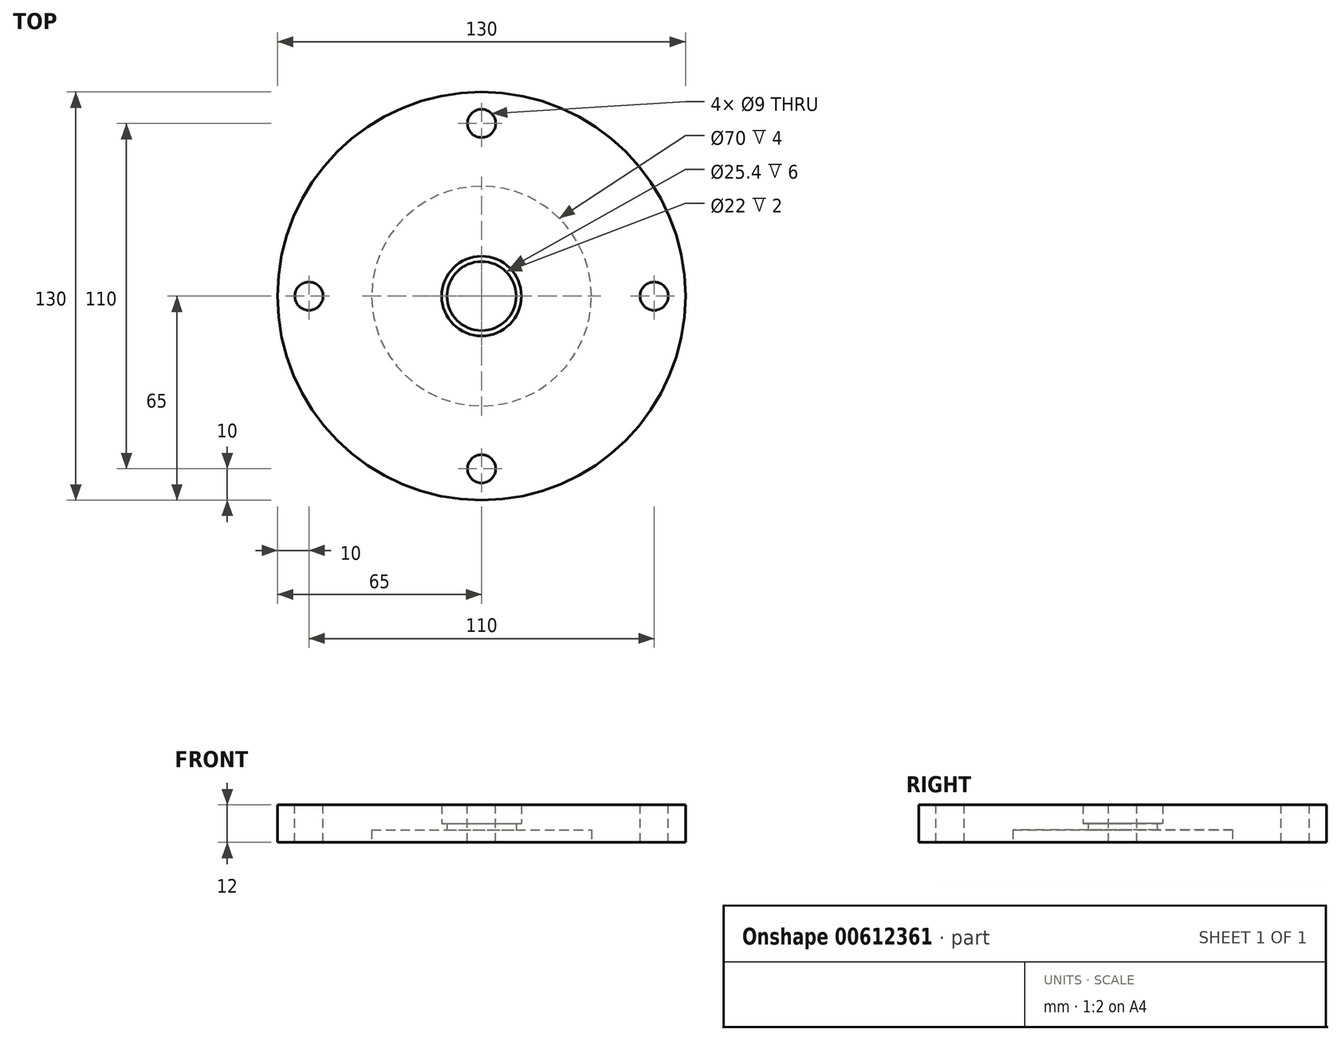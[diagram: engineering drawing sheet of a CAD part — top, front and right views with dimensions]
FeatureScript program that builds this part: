
annotation { "Feature Type Name" : "Feature", "Feature Type Description" : "" }
export const myFeature = defineFeature(function(context is Context, id is Id, definition is map)
    precondition{}
    {
        {
            var Q0;
            Q0=qCreatedBy(makeId("Front.planeOp"),FACE);
            var sketch = newSketch(context, id + "F0", { "sketchPlane" : qUnion([Q0])});
            skLineSegment(sketch, "E0", {"start": v(0, 0) * mm, "end": v(0, 17.2) * mm});
            skLineSegment(sketch, "E1", {"start": v(35, 0) * mm, "end": v(65, 0) * mm});
            skLineSegment(sketch, "E2", {"start": v(65, 0) * mm, "end": v(65, 12) * mm});
            skLineSegment(sketch, "E3", {"start": v(65, 12) * mm, "end": v(12.7, 12) * mm});
            skLineSegment(sketch, "E4", {"start": v(12.7, 12) * mm, "end": v(12.7, 6) * mm});
            skLineSegment(sketch, "E5", {"start": v(11, 6) * mm, "end": v(12.7, 6) * mm});
            skLineSegment(sketch, "E6", {"start": v(11, 6) * mm, "end": v(11, 4) * mm});
            skLineSegment(sketch, "E7", {"start": v(35, 4) * mm, "end": v(11, 4) * mm});
            skLineSegment(sketch, "E8", {"start": v(35, 4) * mm, "end": v(35, 0) * mm});
            skSolve(sketch);
        }
        {
            var Q0;
            Q0=makeQuery(id+"F0.imprint","IMPRINT",FACE,{"disambiguationData":[TD([[makeQuery(id+"F0.imprint","IMPRINT",EDGE,{"derivedFrom":sQuery(id+"F0.wireOp",EDGE,"E1")}),1.0]])]});
            var Q1;
            Q1=sQuery(id+"F0.wireOp",EDGE,"E0");
            revolve(context, id + "F1", {"entities" : qUnion([Q0]), "axis" : qUnion([Q1]), "revolveType" : RevolveType.FULL});
        }
        {
            var Q0;
            Q0=makeQuery(id+"F1.opRevolve","SWEPT_FACE",FACE,{"disambiguationData":[OSD([sQuery(id+"F0.wireOp",EDGE,"E3")])]});
            var sketch = newSketch(context, id + "F2", { "sketchPlane" : qUnion([Q0])});
            skArc(sketch, "E9", {"start": v(54.82, 4.5) * mm, "mid": v(38.9, 38.9) * mm, "end": v(4.5, 54.82) * mm});
            skCircle(sketch, "E10", {"center": v(55, 0) * mm, "radius": 4.5 * mm});
            skCircle(sketch, "E11.1.0", {"center": v(0, 55) * mm, "radius": 4.5 * mm});
            skCircle(sketch, "E11.2.0", {"center": v(-55, 0) * mm, "radius": 4.5 * mm});
            skCircle(sketch, "E11.3.0", {"center": v(0, -55) * mm, "radius": 4.5 * mm});
            skArc(sketch, "E12.trimOffspring", {"start": v(-4.5, 54.82) * mm, "mid": v(-38.9, 38.9) * mm, "end": v(-54.82, 4.5) * mm});
            skArc(sketch, "E13.trimOffspring", {"start": v(-54.82, -4.5) * mm, "mid": v(-38.9, -38.9) * mm, "end": v(-4.5, -54.82) * mm});
            skArc(sketch, "E14.trimOffspring", {"start": v(4.5, -54.82) * mm, "mid": v(38.9, -38.9) * mm, "end": v(54.82, -4.5) * mm});
            skSolve(sketch);
        }
        {
            var Q0;
            {var subQ0=sQuery(id+"F2.wireOp",EDGE,"E11.1.0");var subQ1=makeQuery(id+"F2.imprint","INTERSECT",VERTEX,{"derivedFrom":[sQuery(id+"F2.wireOp",EDGE,"E9"),subQ0]});Q0=makeQuery(id+"F2.imprint","IMPRINT",FACE,{"disambiguationData":[TD([[makeQuery(id+"F2.imprint","IMPRINT",EDGE,{"disambiguationData":[TD([[subQ1,1.0]])],"derivedFrom":subQ0}),1.0]])]});}
            var Q1;
            {var subQ0=sQuery(id+"F2.wireOp",EDGE,"E11.2.0");var subQ1=makeQuery(id+"F2.imprint","INTERSECT",VERTEX,{"derivedFrom":[subQ0,sQuery(id+"F2.wireOp",EDGE,"E12.trimOffspring")]});Q1=makeQuery(id+"F2.imprint","IMPRINT",FACE,{"disambiguationData":[TD([[makeQuery(id+"F2.imprint","IMPRINT",EDGE,{"disambiguationData":[TD([[subQ1,1.0]])],"derivedFrom":subQ0}),1.0]])]});}
            var Q2;
            {var subQ0=sQuery(id+"F2.wireOp",EDGE,"E11.3.0");var subQ1=makeQuery(id+"F2.imprint","INTERSECT",VERTEX,{"derivedFrom":[subQ0,sQuery(id+"F2.wireOp",EDGE,"E13.trimOffspring")]});Q2=makeQuery(id+"F2.imprint","IMPRINT",FACE,{"disambiguationData":[TD([[makeQuery(id+"F2.imprint","IMPRINT",EDGE,{"disambiguationData":[TD([[subQ1,1.0]])],"derivedFrom":subQ0}),1.0]])]});}
            var Q3;
            {var subQ0=sQuery(id+"F2.wireOp",EDGE,"E10");var subQ1=makeQuery(id+"F2.imprint","INTERSECT",VERTEX,{"derivedFrom":[sQuery(id+"F2.wireOp",EDGE,"E9"),subQ0]});Q3=makeQuery(id+"F2.imprint","IMPRINT",FACE,{"disambiguationData":[TD([[makeQuery(id+"F2.imprint","IMPRINT",EDGE,{"disambiguationData":[TD([[subQ1,-1.0]])],"derivedFrom":subQ0}),1.0]])]});}
            extrude(context, id + "F3", {"entities" : qUnion([Q0, Q1, Q2, Q3]), "operationType" : NewBodyOperationType.REMOVE, "oppositeDirection" : true, "depth" : 12 * mm, "offsetDistance" : 25 * mm});
        }
    });
